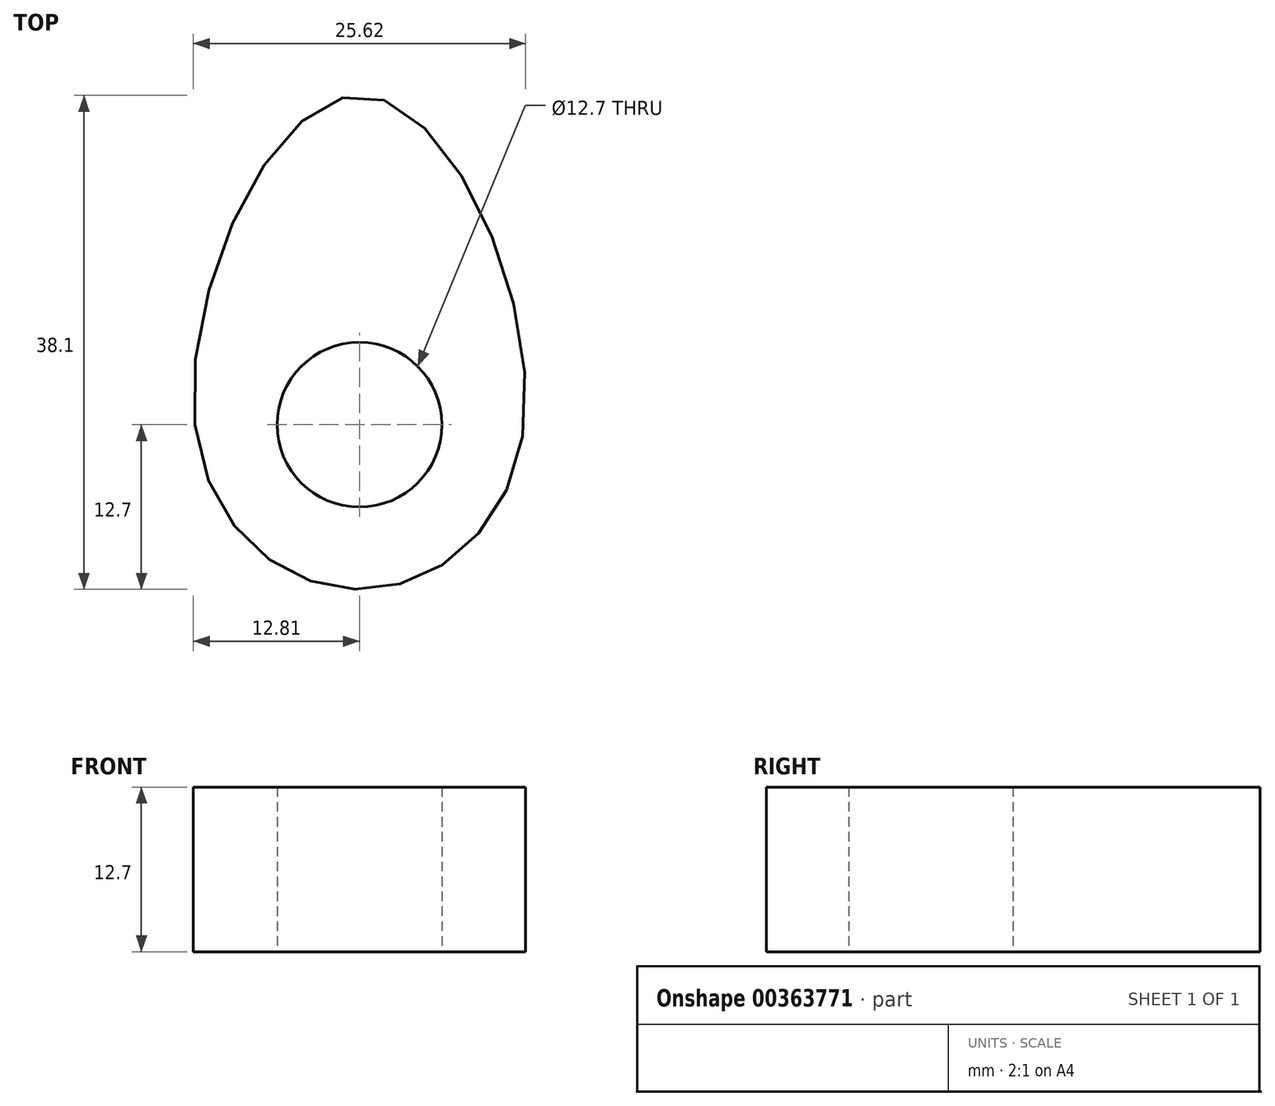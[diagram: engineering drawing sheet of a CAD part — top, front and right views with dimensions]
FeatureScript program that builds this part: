
annotation { "Feature Type Name" : "Feature", "Feature Type Description" : "" }
export const myFeature = defineFeature(function(context is Context, id is Id, definition is map)
    precondition{}
    {
        {
            var Q0;
            Q0=qCreatedBy(makeId("Top.planeOp"),FACE);
            var sketch = newSketch(context, id + "F0", { "sketchPlane" : qUnion([Q0])});
            skCircle(sketch, "E0", {"center": v(0, 0) * mm, "radius": 6.35 * mm});
            skLineSegment(sketch, "E1", {"start": v(-12.7, -12.7) * mm, "end": v(12.7, -12.7) * mm, "construction": true});
            skLineSegment(sketch, "E2", {"start": v(-12.7, 25.4) * mm, "end": v(12.7, 25.4) * mm, "construction": true});
            skLineSegment(sketch, "E3", {"start": v(-12.7, 25.4) * mm, "end": v(-12.7, -12.7) * mm, "construction": true});
            skLineSegment(sketch, "E4", {"start": v(12.7, -12.7) * mm, "end": v(12.7, 25.4) * mm, "construction": true});
            skFitSpline(sketch, "E5", {"points": [v(-12.7, 0) * mm, v(0, 25.4) * mm, v(12.7, 0) * mm, v(0, -12.7) * mm, v(-12.7, 0) * mm]});
            skSolve(sketch);
        }
        {
            var Q0;
            Q0=makeQuery(id+"F0.imprint","IMPRINT",FACE,{"disambiguationData":[TD([[makeQuery(id+"F0.imprint","IMPRINT",EDGE,{"derivedFrom":sQuery(id+"F0.wireOp",EDGE,"E0")}),-1.0]])]});
            extrude(context, id + "F1", {"entities" : qUnion([Q0]), "depth" : 12.7 * mm});
        }
    });
